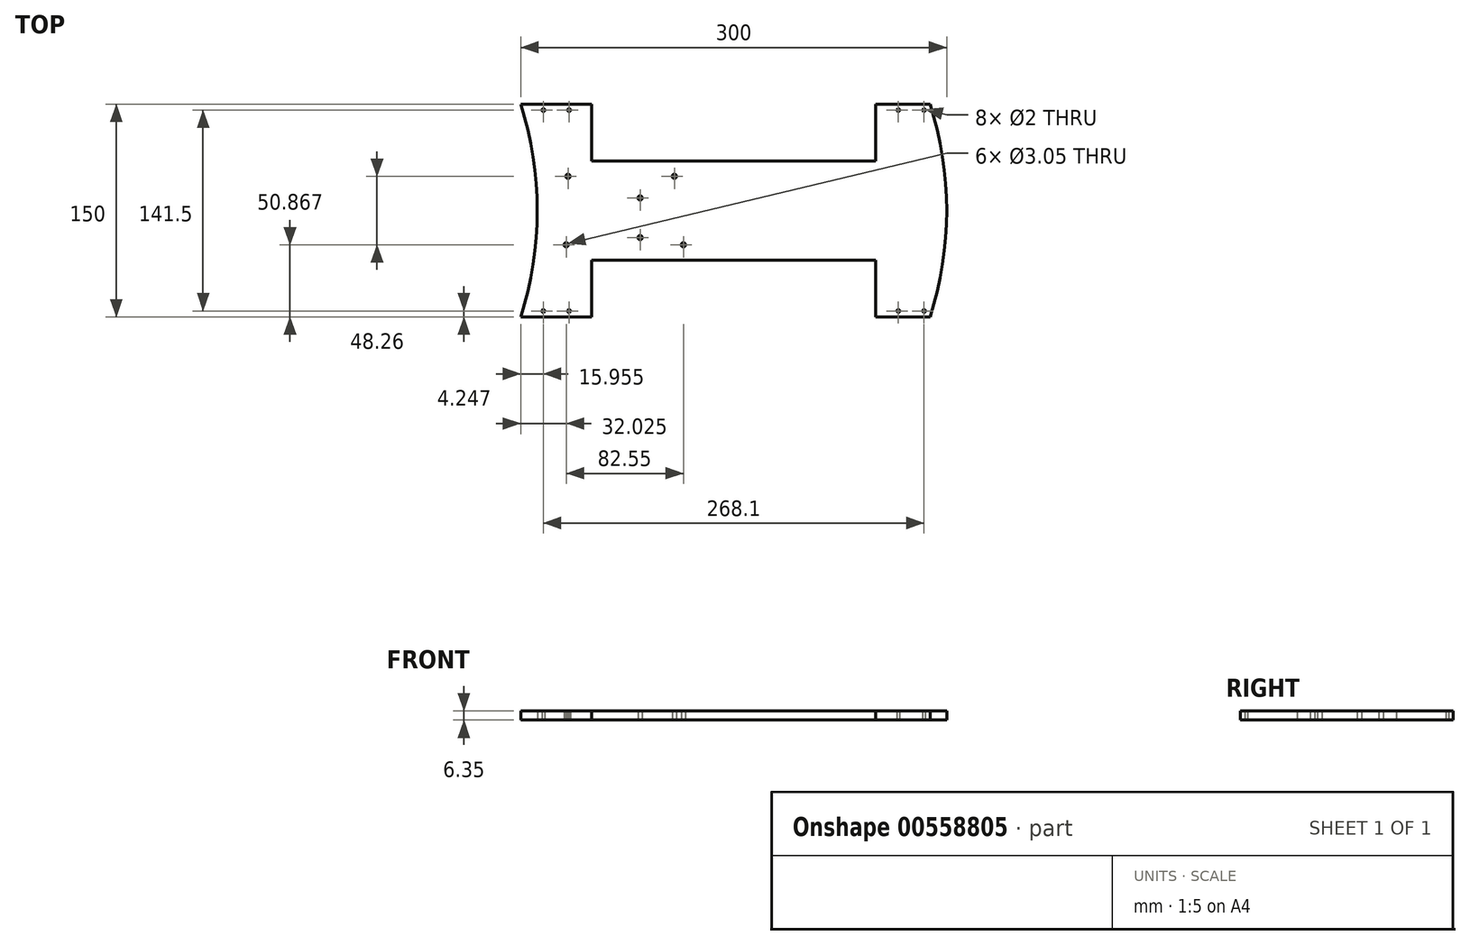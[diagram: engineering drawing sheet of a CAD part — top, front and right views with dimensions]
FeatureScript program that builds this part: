
annotation { "Feature Type Name" : "Feature", "Feature Type Description" : "" }
export const myFeature = defineFeature(function(context is Context, id is Id, definition is map)
    precondition{}
    {
        {
            var Q0;
            Q0=qCreatedBy(makeId("Top.planeOp"),FACE);
            var sketch = newSketch(context, id + "F0", { "sketchPlane" : qUnion([Q0])});
            skCircle(sketch, "E0", {"center": v(-163.1, -14.42) * mm, "radius": 1.52 * mm});
            skCircle(sketch, "E1", {"center": v(-164.38, -62.68) * mm, "radius": 1.52 * mm});
            skCircle(sketch, "E2", {"center": v(-112.3, -57.6) * mm, "radius": 1.52 * mm});
            skCircle(sketch, "E3", {"center": v(-112.3, -29.66) * mm, "radius": 1.52 * mm});
            skCircle(sketch, "E4", {"center": v(-88.18, -14.42) * mm, "radius": 1.52 * mm});
            skCircle(sketch, "E5", {"center": v(-81.83, -62.68) * mm, "radius": 1.52 * mm});
            skLineSegment(sketch, "E6.bottom", {"start": v(-196.4, -113.55) * mm, "end": v(91.9, -113.55) * mm});
            skLineSegment(sketch, "E6.top", {"start": v(-196.4, 36.45) * mm, "end": v(103.6, 36.45) * mm});
            skLineSegment(sketch, "E7", {"start": v(-146.4, 36.45) * mm, "end": v(-146.4, -3.55) * mm});
            skLineSegment(sketch, "E8", {"start": v(-146.4, -3.55) * mm, "end": v(53.6, -3.55) * mm});
            skLineSegment(sketch, "E9", {"start": v(53.6, -3.55) * mm, "end": v(53.6, 36.45) * mm});
            skLineSegment(sketch, "E10.top", {"start": v(-184.7, 36.45) * mm, "end": v(-158.1, 36.45) * mm});
            skLineSegment(sketch, "E10.left", {"start": v(-184.7, 27.95) * mm, "end": v(-184.7, 36.45) * mm});
            skCircle(sketch, "E11", {"center": v(-180.45, 32.2) * mm, "radius": 1 * mm});
            skCircle(sketch, "E12", {"center": v(-162.35, 32.2) * mm, "radius": 1 * mm});
            skLineSegment(sketch, "E13.top", {"start": v(65.3, 36.45) * mm, "end": v(91.9, 36.45) * mm});
            skCircle(sketch, "E14", {"center": v(69.55, 32.2) * mm, "radius": 1 * mm});
            skCircle(sketch, "E15", {"center": v(87.65, 32.2) * mm, "radius": 1 * mm});
            skLineSegment(sketch, "E16.MirrorCS", {"start": v(-146.4, -113.55) * mm, "end": v(-146.4, -73.55) * mm});
            skLineSegment(sketch, "E17.MirrorCS", {"start": v(-146.4, -73.55) * mm, "end": v(53.6, -73.55) * mm});
            skLineSegment(sketch, "E18.MirrorCS", {"start": v(53.6, -73.55) * mm, "end": v(53.6, -113.55) * mm});
            skCircle(sketch, "E19.MirrorC", {"center": v(69.55, -109.3) * mm, "radius": 1 * mm});
            skCircle(sketch, "E20.MirrorC", {"center": v(87.65, -109.3) * mm, "radius": 1 * mm});
            skCircle(sketch, "E21.MirrorC", {"center": v(-162.35, -109.3) * mm, "radius": 1 * mm});
            skCircle(sketch, "E22.MirrorC", {"center": v(-180.45, -109.3) * mm, "radius": 1 * mm});
            skArc(sketch, "E23", {"start": v(-196.4, -113.55) * mm, "mid": v(-184.7, -38.55) * mm, "end": v(-196.4, 36.45) * mm});
            skArc(sketch, "E24", {"start": v(91.9, -113.55) * mm, "mid": v(103.6, -38.55) * mm, "end": v(91.9, 36.45) * mm});
            skLineSegment(sketch, "E25.trimOffspring", {"start": v(103.6, 35.74) * mm, "end": v(103.6, 36.45) * mm});
            skSolve(sketch);
        }
        {
            var Q0;
            Q0=makeQuery(id+"F0.imprint","IMPRINT",FACE,{"disambiguationData":[TD([[makeQuery(id+"F0.imprint","IMPRINT",EDGE,{"derivedFrom":sQuery(id+"F0.wireOp",EDGE,"E0")}),-1.0]])]});
            extrude(context, id + "F1", {"entities" : qUnion([Q0]), "depth" : 6.35 * mm, "offsetDistance" : 25.4 * mm});
        }
    });
